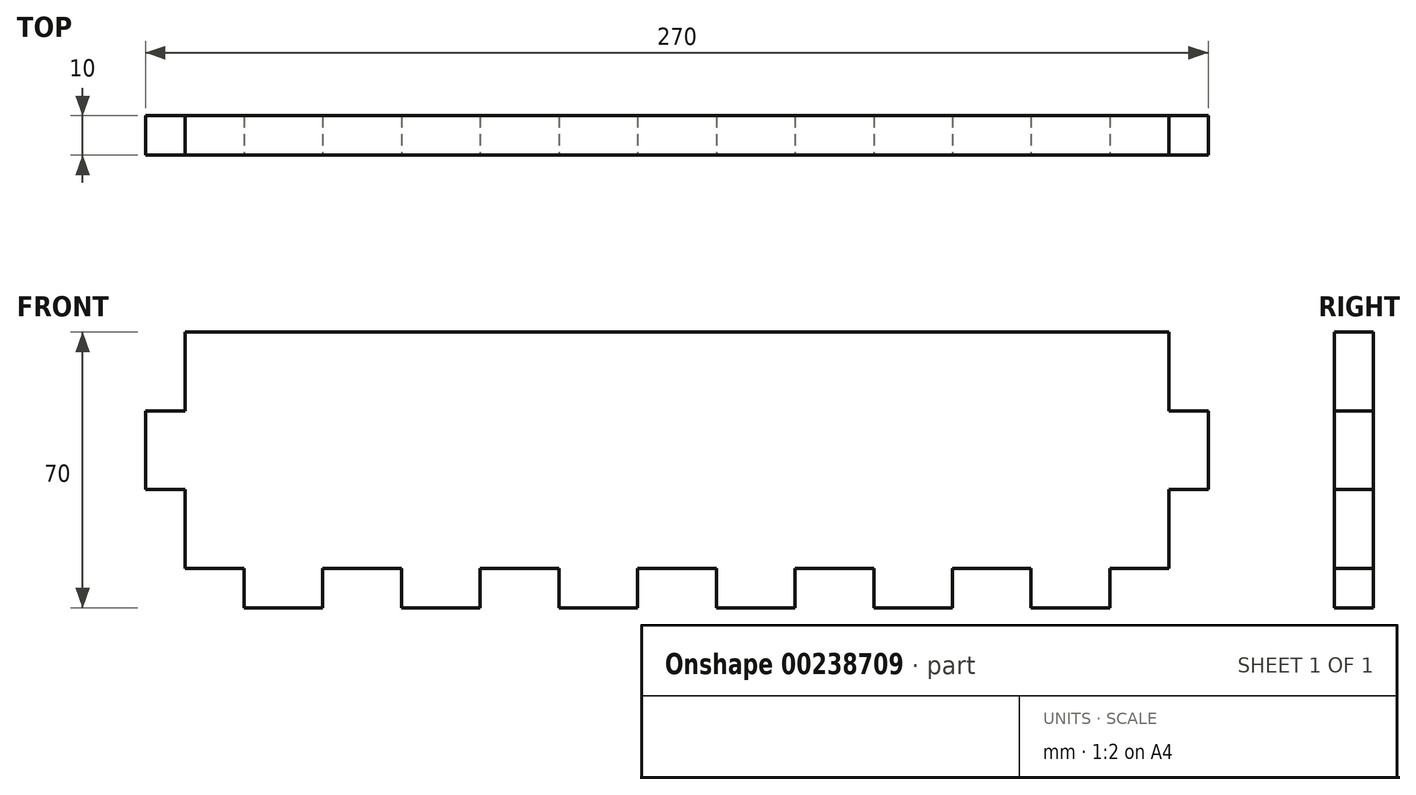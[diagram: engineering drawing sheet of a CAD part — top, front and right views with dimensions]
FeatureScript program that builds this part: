
annotation { "Feature Type Name" : "Feature", "Feature Type Description" : "" }
export const myFeature = defineFeature(function(context is Context, id is Id, definition is map)
    precondition{}
    {
        {
            var Q0;
            Q0=qCreatedBy(makeId("Front.planeOp"),FACE);
            var sketch = newSketch(context, id + "F0", { "sketchPlane" : qUnion([Q0])});
            skLineSegment(sketch, "E0.bottom", {"start": v(0, -100) * mm, "end": v(250, -100) * mm, "construction": true});
            skLineSegment(sketch, "E0.top", {"start": v(0, 40) * mm, "end": v(250, 40) * mm, "construction": true});
            skLineSegment(sketch, "E0.right", {"start": v(250, -100) * mm, "end": v(250, 40) * mm, "construction": true});
            skLineSegment(sketch, "E1", {"start": v(125, -92.5) * mm, "end": v(125, -100) * mm, "construction": true});
            skLineSegment(sketch, "E2.top", {"start": v(135, -110) * mm, "end": v(115, -110) * mm});
            skLineSegment(sketch, "E2.left", {"start": v(135, -100) * mm, "end": v(135, -110) * mm});
            skLineSegment(sketch, "E2.right", {"start": v(115, -100) * mm, "end": v(115, -110) * mm});
            skPoint(sketch, "E2.middle", {"position": v(125, -105) * mm});
            skLineSegment(sketch, "E3", {"start": v(135, -100) * mm, "end": v(155, -100) * mm});
            skLineSegment(sketch, "E4.1.0.0", {"start": v(155, -100) * mm, "end": v(155, -110) * mm});
            skLineSegment(sketch, "E4.1.0.1", {"start": v(175, -110) * mm, "end": v(155, -110) * mm});
            skLineSegment(sketch, "E4.1.0.2", {"start": v(175, -100) * mm, "end": v(175, -110) * mm});
            skLineSegment(sketch, "E4.1.0.3", {"start": v(175, -100) * mm, "end": v(195, -100) * mm});
            skLineSegment(sketch, "E4.2.0.0", {"start": v(195, -100) * mm, "end": v(195, -110) * mm});
            skLineSegment(sketch, "E4.2.0.1", {"start": v(215, -110) * mm, "end": v(195, -110) * mm});
            skLineSegment(sketch, "E4.2.0.2", {"start": v(215, -100) * mm, "end": v(215, -110) * mm});
            skLineSegment(sketch, "E4.2.0.3", {"start": v(215, -100) * mm, "end": v(235, -100) * mm});
            skLineSegment(sketch, "E4.direction1", {"start": v(115, -110) * mm, "end": v(155, -110) * mm, "construction": true});
            skLineSegment(sketch, "E5.0.3.0", {"start": v(235, -100) * mm, "end": v(235, -110) * mm});
            skLineSegment(sketch, "E6.MirrorCS", {"start": v(15, -100) * mm, "end": v(15, -110) * mm});
            skLineSegment(sketch, "E7.MirrorCS", {"start": v(35, -100) * mm, "end": v(35, -110) * mm});
            skLineSegment(sketch, "E8.MirrorCS", {"start": v(35, -110) * mm, "end": v(55, -110) * mm});
            skLineSegment(sketch, "E9.MirrorCS", {"start": v(55, -100) * mm, "end": v(55, -110) * mm});
            skLineSegment(sketch, "E10.MirrorCS", {"start": v(75, -100) * mm, "end": v(75, -110) * mm});
            skLineSegment(sketch, "E11.MirrorCS", {"start": v(75, -110) * mm, "end": v(95, -110) * mm});
            skLineSegment(sketch, "E12.MirrorCS", {"start": v(95, -100) * mm, "end": v(95, -110) * mm});
            skLineSegment(sketch, "E13.MirrorCS", {"start": v(35, -100) * mm, "end": v(15, -100) * mm});
            skLineSegment(sketch, "E14.MirrorCS", {"start": v(115, -100) * mm, "end": v(95, -100) * mm});
            skLineSegment(sketch, "E15.MirrorCS", {"start": v(75, -100) * mm, "end": v(55, -100) * mm});
            skLineSegment(sketch, "E16.bottom", {"start": v(250, -20) * mm, "end": v(260, -20) * mm});
            skLineSegment(sketch, "E16.top", {"start": v(250, -40) * mm, "end": v(260, -40) * mm});
            skLineSegment(sketch, "E16.right", {"start": v(260, -20) * mm, "end": v(260, -40) * mm});
            skPoint(sketch, "E16.middle", {"position": v(255, -30) * mm});
            skPoint(sketch, "E16.middle.positionSnap0", {"position": v(250, -30) * mm});
            skPoint(sketch, "E16.centerSnap0", {"position": v(250, -30) * mm});
            skLineSegment(sketch, "E17", {"start": v(250, -20) * mm, "end": v(250, 0) * mm});
            skLineSegment(sketch, "E18.0.1.0", {"start": v(250, 0) * mm, "end": v(260, 0) * mm});
            skLineSegment(sketch, "E18.0.1.1", {"start": v(260, 20) * mm, "end": v(260, 0) * mm});
            skLineSegment(sketch, "E18.0.1.2", {"start": v(250, 20) * mm, "end": v(260, 20) * mm});
            skLineSegment(sketch, "E18.0.1.3", {"start": v(250, 20) * mm, "end": v(250, 40) * mm});
            skLineSegment(sketch, "E18.0.2.0", {"start": v(250, 40) * mm, "end": v(260, 40) * mm});
            skLineSegment(sketch, "E18.direction1", {"start": v(250, -40) * mm, "end": v(275, -40) * mm, "construction": true});
            skLineSegment(sketch, "E18.direction2", {"start": v(250, -40) * mm, "end": v(250, 0) * mm, "construction": true});
            skLineSegment(sketch, "E19", {"start": v(255, -30) * mm, "end": v(250, -30) * mm, "construction": true});
            skLineSegment(sketch, "E20.MirrorCS", {"start": v(250, -40) * mm, "end": v(250, -60) * mm});
            skLineSegment(sketch, "E21.MirrorCS", {"start": v(250, -60) * mm, "end": v(260, -60) * mm});
            skLineSegment(sketch, "E22.MirrorCS", {"start": v(260, -80) * mm, "end": v(260, -60) * mm});
            skLineSegment(sketch, "E23.MirrorCS", {"start": v(250, -80) * mm, "end": v(260, -80) * mm});
            skLineSegment(sketch, "E24.MirrorCS", {"start": v(250, -80) * mm, "end": v(250, -100) * mm});
            skLineSegment(sketch, "E25.MirrorCS", {"start": v(250, -100) * mm, "end": v(260, -100) * mm});
            skLineSegment(sketch, "E26", {"start": v(235, -110) * mm, "end": v(260, -110) * mm});
            skLineSegment(sketch, "E27", {"start": v(260, -110) * mm, "end": v(260, -100) * mm});
            skLineSegment(sketch, "E28.MirrorCS", {"start": v(35, 40) * mm, "end": v(35, 50) * mm});
            skLineSegment(sketch, "E29.MirrorCS", {"start": v(115, 40) * mm, "end": v(115, 50) * mm});
            skLineSegment(sketch, "E30.MirrorCS", {"start": v(55, 40) * mm, "end": v(55, 50) * mm});
            skLineSegment(sketch, "E31.MirrorCS", {"start": v(155, 40) * mm, "end": v(155, 50) * mm});
            skLineSegment(sketch, "E32.MirrorCS", {"start": v(75, 40) * mm, "end": v(75, 50) * mm});
            skLineSegment(sketch, "E33.MirrorCS", {"start": v(235, 40) * mm, "end": v(235, 50) * mm});
            skLineSegment(sketch, "E34.MirrorCS", {"start": v(95, 40) * mm, "end": v(95, 50) * mm});
            skLineSegment(sketch, "E35.MirrorCS", {"start": v(15, 40) * mm, "end": v(15, 50) * mm});
            skLineSegment(sketch, "E36.MirrorCS", {"start": v(260, 50) * mm, "end": v(260, 40) * mm});
            skLineSegment(sketch, "E37.MirrorCS", {"start": v(175, 40) * mm, "end": v(175, 50) * mm});
            skLineSegment(sketch, "E38.MirrorCS", {"start": v(195, 40) * mm, "end": v(195, 50) * mm});
            skLineSegment(sketch, "E39.MirrorCS", {"start": v(135, 40) * mm, "end": v(135, 50) * mm});
            skLineSegment(sketch, "E40.MirrorCS", {"start": v(215, 40) * mm, "end": v(215, 50) * mm});
            skLineSegment(sketch, "E41.MirrorCS", {"start": v(135, 40) * mm, "end": v(155, 40) * mm});
            skLineSegment(sketch, "E42.MirrorCS", {"start": v(215, 40) * mm, "end": v(235, 40) * mm});
            skLineSegment(sketch, "E43.MirrorCS", {"start": v(175, 40) * mm, "end": v(195, 40) * mm});
            skLineSegment(sketch, "E44.MirrorCS", {"start": v(35, 40) * mm, "end": v(15, 40) * mm});
            skLineSegment(sketch, "E45.MirrorCS", {"start": v(115, 40) * mm, "end": v(95, 40) * mm});
            skLineSegment(sketch, "E46.MirrorCS", {"start": v(75, 40) * mm, "end": v(55, 40) * mm});
            skLineSegment(sketch, "E47.MirrorCS", {"start": v(135, 50) * mm, "end": v(115, 50) * mm});
            skLineSegment(sketch, "E48.MirrorCS", {"start": v(35, 50) * mm, "end": v(55, 50) * mm});
            skLineSegment(sketch, "E49.MirrorCS", {"start": v(175, 50) * mm, "end": v(155, 50) * mm});
            skLineSegment(sketch, "E50.MirrorCS", {"start": v(215, 50) * mm, "end": v(195, 50) * mm});
            skLineSegment(sketch, "E51.MirrorCS", {"start": v(75, 50) * mm, "end": v(95, 50) * mm});
            skLineSegment(sketch, "E52.MirrorCS", {"start": v(235, 50) * mm, "end": v(260, 50) * mm});
            skLineSegment(sketch, "E53.MirrorCS", {"start": v(15, -110) * mm, "end": v(-10, -110) * mm});
            skLineSegment(sketch, "E54.MirrorCS", {"start": v(-10, -110) * mm, "end": v(-10, -100) * mm});
            skLineSegment(sketch, "E55.MirrorCS", {"start": v(0, -100) * mm, "end": v(-10, -100) * mm});
            skLineSegment(sketch, "E56.MirrorCS", {"start": v(0, -80) * mm, "end": v(-10, -80) * mm});
            skLineSegment(sketch, "E57.MirrorCS", {"start": v(-10, -80) * mm, "end": v(-10, -60) * mm});
            skLineSegment(sketch, "E58.MirrorCS", {"start": v(0, -60) * mm, "end": v(-10, -60) * mm});
            skLineSegment(sketch, "E59.MirrorCS", {"start": v(0, -100) * mm, "end": v(0, 40) * mm, "construction": true});
            skLineSegment(sketch, "E60.MirrorCS", {"start": v(-10, -20) * mm, "end": v(-10, -40) * mm, "construction": true});
            skLineSegment(sketch, "E61.MirrorCS", {"start": v(0, -20) * mm, "end": v(-10, -20) * mm});
            skLineSegment(sketch, "E62.MirrorCS", {"start": v(0, 0) * mm, "end": v(-10, 0) * mm});
            skLineSegment(sketch, "E63.MirrorCS", {"start": v(-10, 20) * mm, "end": v(-10, 0) * mm});
            skLineSegment(sketch, "E64.MirrorCS", {"start": v(0, 20) * mm, "end": v(-10, 20) * mm});
            skLineSegment(sketch, "E65.MirrorCS", {"start": v(0, 40) * mm, "end": v(-10, 40) * mm});
            skLineSegment(sketch, "E66.MirrorCS", {"start": v(-10, 50) * mm, "end": v(-10, 40) * mm});
            skLineSegment(sketch, "E67.MirrorCS", {"start": v(0, 20) * mm, "end": v(0, 40) * mm});
            skLineSegment(sketch, "E68.MirrorCS", {"start": v(0, -20) * mm, "end": v(0, 0) * mm});
            skLineSegment(sketch, "E69.MirrorCS", {"start": v(0, -40) * mm, "end": v(0, -60) * mm});
            skLineSegment(sketch, "E70.MirrorCS", {"start": v(0, -80) * mm, "end": v(0, -100) * mm});
            skLineSegment(sketch, "E71.MirrorCS", {"start": v(0, -40) * mm, "end": v(-10, -40) * mm});
            skLineSegment(sketch, "E72", {"start": v(-10, 50) * mm, "end": v(15, 50) * mm});
            skLineSegment(sketch, "E73.bottom", {"start": v(-10, -110) * mm, "end": v(260, -110) * mm, "construction": true});
            skLineSegment(sketch, "E73.top", {"start": v(-10, -230) * mm, "end": v(260, -230) * mm});
            skLineSegment(sketch, "E73.left", {"start": v(-10, -110) * mm, "end": v(-10, -230) * mm, "construction": true});
            skLineSegment(sketch, "E73.right", {"start": v(260, -110) * mm, "end": v(260, -230) * mm, "construction": true});
            skLineSegment(sketch, "E74.bottom", {"start": v(260, 50) * mm, "end": v(-10, 50) * mm, "construction": true});
            skLineSegment(sketch, "E74.top", {"start": v(260, 110) * mm, "end": v(-10, 110) * mm});
            skLineSegment(sketch, "E74.left", {"start": v(260, 50) * mm, "end": v(260, 110) * mm, "construction": true});
            skLineSegment(sketch, "E74.right", {"start": v(-10, 50) * mm, "end": v(-10, 110) * mm, "construction": true});
            skLineSegment(sketch, "E75.bottom", {"start": v(260, 40) * mm, "end": v(320, 40) * mm, "construction": true});
            skLineSegment(sketch, "E75.top", {"start": v(260, -100) * mm, "end": v(380, -100) * mm, "construction": true});
            skLineSegment(sketch, "E75.right", {"start": v(320, 40) * mm, "end": v(380, -100) * mm});
            skLineSegment(sketch, "E76.top", {"start": v(260, -110) * mm, "end": v(280, -110) * mm});
            skLineSegment(sketch, "E76.left", {"start": v(260, -100) * mm, "end": v(260, -110) * mm});
            skLineSegment(sketch, "E76.right", {"start": v(280, -100) * mm, "end": v(280, -110) * mm});
            skLineSegment(sketch, "E77", {"start": v(280, -100) * mm, "end": v(300, -100) * mm});
            skLineSegment(sketch, "E78.1.0.0", {"start": v(320, -100) * mm, "end": v(340, -100) * mm});
            skLineSegment(sketch, "E78.1.0.1", {"start": v(320, -100) * mm, "end": v(320, -110) * mm});
            skLineSegment(sketch, "E78.1.0.2", {"start": v(300, -110) * mm, "end": v(320, -110) * mm});
            skLineSegment(sketch, "E78.1.0.3", {"start": v(300, -100) * mm, "end": v(300, -110) * mm});
            skLineSegment(sketch, "E78.2.0.0", {"start": v(360, -100) * mm, "end": v(380, -100) * mm});
            skLineSegment(sketch, "E78.2.0.1", {"start": v(360, -100) * mm, "end": v(360, -110) * mm});
            skLineSegment(sketch, "E78.2.0.2", {"start": v(340, -110) * mm, "end": v(360, -110) * mm});
            skLineSegment(sketch, "E78.2.0.3", {"start": v(340, -100) * mm, "end": v(340, -110) * mm});
            skLineSegment(sketch, "E78.direction1", {"start": v(260, -110) * mm, "end": v(300, -110) * mm, "construction": true});
            skLineSegment(sketch, "E79.top", {"start": v(250, -110) * mm, "end": v(250, -130) * mm});
            skLineSegment(sketch, "E79.left", {"start": v(260, -110) * mm, "end": v(250, -110) * mm});
            skLineSegment(sketch, "E79.right", {"start": v(260, -130) * mm, "end": v(250, -130) * mm});
            skLineSegment(sketch, "E80", {"start": v(260, -130) * mm, "end": v(260, -150) * mm});
            skLineSegment(sketch, "E81.1.0.0", {"start": v(260, -170) * mm, "end": v(260, -190) * mm});
            skLineSegment(sketch, "E81.1.0.1", {"start": v(260, -170) * mm, "end": v(250, -170) * mm});
            skLineSegment(sketch, "E81.1.0.2", {"start": v(250, -150) * mm, "end": v(250, -170) * mm});
            skLineSegment(sketch, "E81.1.0.3", {"start": v(260, -150) * mm, "end": v(250, -150) * mm});
            skLineSegment(sketch, "E81.2.0.0", {"start": v(260, -210) * mm, "end": v(260, -230) * mm});
            skLineSegment(sketch, "E81.2.0.1", {"start": v(260, -210) * mm, "end": v(250, -210) * mm});
            skLineSegment(sketch, "E81.2.0.2", {"start": v(250, -190) * mm, "end": v(250, -210) * mm});
            skLineSegment(sketch, "E81.2.0.3", {"start": v(260, -190) * mm, "end": v(250, -190) * mm});
            skLineSegment(sketch, "E81.direction1", {"start": v(250, -110) * mm, "end": v(250, -150) * mm, "construction": true});
            skLineSegment(sketch, "E82.MirrorCS", {"start": v(280, 40) * mm, "end": v(280, 50) * mm});
            skLineSegment(sketch, "E83.MirrorCS", {"start": v(280, 40) * mm, "end": v(300, 40) * mm});
            skLineSegment(sketch, "E84.MirrorCS", {"start": v(300, 40) * mm, "end": v(300, 50) * mm});
            skLineSegment(sketch, "E85.MirrorCS", {"start": v(300, 50) * mm, "end": v(320, 50) * mm});
            skLineSegment(sketch, "E86.MirrorCS", {"start": v(320, 40) * mm, "end": v(320, 50) * mm, "construction": true});
            skLineSegment(sketch, "E87.MirrorCS", {"start": v(260, 40) * mm, "end": v(260, 50) * mm});
            skLineSegment(sketch, "E88.MirrorCS", {"start": v(260, 50) * mm, "end": v(280, 50) * mm});
            skLineSegment(sketch, "E89.MirrorCS", {"start": v(250, 50) * mm, "end": v(250, 70) * mm});
            skLineSegment(sketch, "E90.MirrorCS", {"start": v(260, 70) * mm, "end": v(250, 70) * mm});
            skLineSegment(sketch, "E91.MirrorCS", {"start": v(260, 70) * mm, "end": v(260, 90) * mm});
            skLineSegment(sketch, "E92.MirrorCS", {"start": v(260, 90) * mm, "end": v(250, 90) * mm});
            skLineSegment(sketch, "E93.MirrorCS", {"start": v(250, 90) * mm, "end": v(250, 110) * mm});
            skLineSegment(sketch, "E94.MirrorCS", {"start": v(-10, -210) * mm, "end": v(-10, -230) * mm});
            skLineSegment(sketch, "E95.MirrorCS", {"start": v(-10, -210) * mm, "end": v(0, -210) * mm});
            skLineSegment(sketch, "E96.MirrorCS", {"start": v(0, -190) * mm, "end": v(0, -210) * mm});
            skLineSegment(sketch, "E97.MirrorCS", {"start": v(-10, -190) * mm, "end": v(0, -190) * mm});
            skLineSegment(sketch, "E98.MirrorCS", {"start": v(-10, -170) * mm, "end": v(-10, -190) * mm});
            skLineSegment(sketch, "E99.MirrorCS", {"start": v(-10, -170) * mm, "end": v(0, -170) * mm});
            skLineSegment(sketch, "E100.MirrorCS", {"start": v(0, -150) * mm, "end": v(0, -170) * mm});
            skLineSegment(sketch, "E101.MirrorCS", {"start": v(-10, -150) * mm, "end": v(0, -150) * mm});
            skLineSegment(sketch, "E102.MirrorCS", {"start": v(-10, -130) * mm, "end": v(-10, -150) * mm});
            skLineSegment(sketch, "E103.MirrorCS", {"start": v(-10, -130) * mm, "end": v(0, -130) * mm});
            skLineSegment(sketch, "E104.MirrorCS", {"start": v(0, -110) * mm, "end": v(0, -150) * mm, "construction": true});
            skLineSegment(sketch, "E105.MirrorCS", {"start": v(0, -110) * mm, "end": v(0, -130) * mm});
            skLineSegment(sketch, "E106.MirrorCS", {"start": v(0, 50) * mm, "end": v(0, 70) * mm});
            skLineSegment(sketch, "E107.MirrorCS", {"start": v(-10, 70) * mm, "end": v(0, 70) * mm});
            skLineSegment(sketch, "E108.MirrorCS", {"start": v(-10, 70) * mm, "end": v(-10, 90) * mm});
            skLineSegment(sketch, "E109.MirrorCS", {"start": v(-10, 90) * mm, "end": v(0, 90) * mm});
            skLineSegment(sketch, "E110.MirrorCS", {"start": v(0, 90) * mm, "end": v(0, 110) * mm});
            skLineSegment(sketch, "E111", {"start": v(320, 40) * mm, "end": v(315.71, 50) * mm});
            skSolve(sketch);
        }
        {
            var Q0;
            Q0=makeQuery(id+"F0.imprint","IMPRINT",FACE,{"disambiguationData":[TD([[makeQuery(id+"F0.imprint","IMPRINT",EDGE,{"derivedFrom":sQuery(id+"F0.wireOp",EDGE,"6DD6EAd9-EjR4-M54x-3Gs5-ZzkpjLEBHBt8.bottom")}),1.0]])]});
            var Q1;
            Q1=makeQuery(id+"F0.imprint","IMPRINT",FACE,{"disambiguationData":[TD([[makeQuery(id+"F0.imprint","IMPRINT",EDGE,{"derivedFrom":sQuery(id+"F0.wireOp",EDGE,"3aa721ca-eb7f-4933-b860-b67e4f9833b7.bottom")}),1.0]])]});
            var Q2;
            Q2=makeQuery(id+"F0.imprint","IMPRINT",FACE,{"disambiguationData":[TD([[makeQuery(id+"F0.imprint","IMPRINT",EDGE,{"derivedFrom":sQuery(id+"F0.wireOp",EDGE,"1f1aca45-ddc4-4c07-b0ce-2f99aba2689f.bottom")}),1.0]])]});
            var Q3;
            Q3=makeQuery(id+"F0.imprint","IMPRINT",FACE,{"disambiguationData":[TD([[makeQuery(id+"F0.imprint","IMPRINT",EDGE,{"derivedFrom":sQuery(id+"F0.wireOp",EDGE,"cb640f68-ba69-4848-84fb-c352f3b5514c.1.0.0")}),-1.0]])]});
            var Q4;
            Q4=makeQuery(id+"F0.imprint","IMPRINT",FACE,{"disambiguationData":[TD([[makeQuery(id+"F0.imprint","IMPRINT",EDGE,{"derivedFrom":sQuery(id+"F0.wireOp",EDGE,"be0e698b-39bb-4470-8cd3-9eb53d7fa9ec.3.0.4")}),-1.0]])]});
            var Q5;
            Q5=makeQuery(id+"F0.imprint","IMPRINT",FACE,{"disambiguationData":[TD([[makeQuery(id+"F0.imprint","IMPRINT",EDGE,{"derivedFrom":sQuery(id+"F0.wireOp",EDGE,"be0e698b-39bb-4470-8cd3-9eb53d7fa9ec.2.0.4")}),-1.0]])]});
            var Q6;
            Q6=makeQuery(id+"F0.imprint","IMPRINT",FACE,{"disambiguationData":[TD([[makeQuery(id+"F0.imprint","IMPRINT",EDGE,{"derivedFrom":sQuery(id+"F0.wireOp",EDGE,"be0e698b-39bb-4470-8cd3-9eb53d7fa9ec.1.0.4")}),-1.0]])]});
            var Q7;
            Q7=makeQuery(id+"F0.imprint","IMPRINT",FACE,{"disambiguationData":[TD([[makeQuery(id+"F0.imprint","IMPRINT",EDGE,{"derivedFrom":sQuery(id+"F0.wireOp",EDGE,"KLXXNCfZ-N2lI-LQPs-WN5Q-R0OJi47yWmJK")}),-1.0]])]});
            var Q8;
            Q8=makeQuery(id+"F0.imprint","IMPRINT",FACE,{"disambiguationData":[TD([[makeQuery(id+"F0.imprint","IMPRINT",EDGE,{"derivedFrom":sQuery(id+"F0.wireOp",EDGE,"E28.MirrorCS")}),1.0]])]});
            extrude(context, id + "F1", {"entities" : qUnion([Q0, Q1, Q2, Q3, Q4, Q5, Q6, Q7, Q8]), "oppositeDirection" : true, "depth" : 10 * mm});
        }
    });
